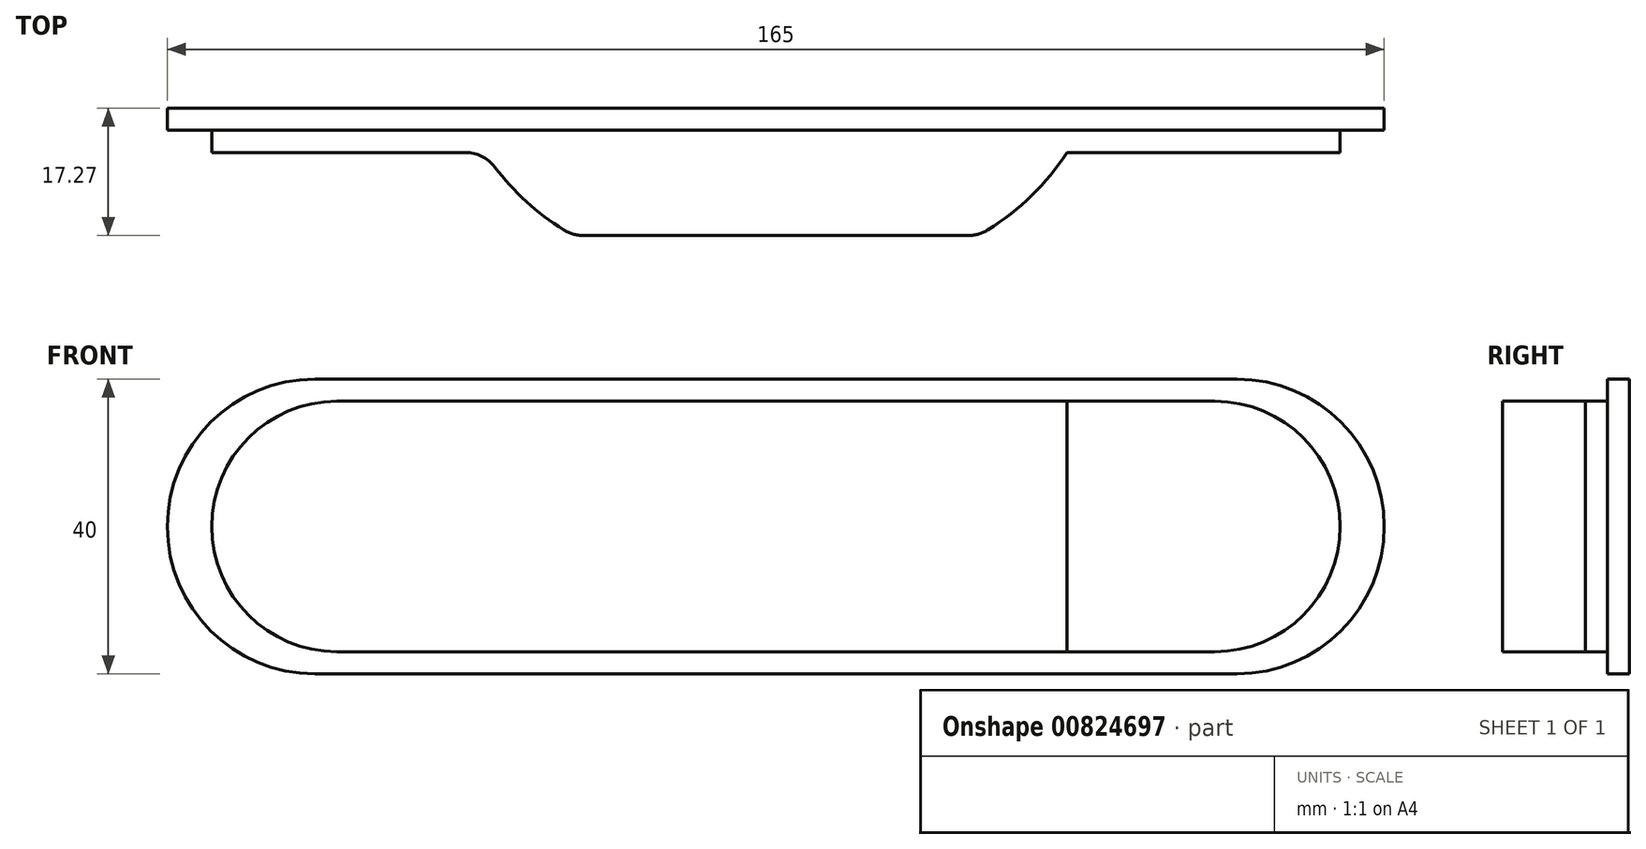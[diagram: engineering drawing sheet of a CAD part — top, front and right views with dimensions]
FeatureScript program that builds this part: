
annotation { "Feature Type Name" : "Feature", "Feature Type Description" : "" }
export const myFeature = defineFeature(function(context is Context, id is Id, definition is map)
    precondition{}
    {
        {
            var Q0;
            Q0=qCreatedBy(makeId("Front.planeOp"),FACE);
            var sketch = newSketch(context, id + "F0", { "sketchPlane" : qUnion([Q0])});
            skLineSegment(sketch, "E0.bottom", {"start": v(62.5, 20) * mm, "end": v(-62.5, 20) * mm});
            skLineSegment(sketch, "E0.top", {"start": v(62.5, -20) * mm, "end": v(-62.5, -20) * mm});
            skLineSegment(sketch, "E0.left", {"start": v(62.5, 20) * mm, "end": v(62.5, -20) * mm});
            skLineSegment(sketch, "E0.right", {"start": v(-62.5, 20) * mm, "end": v(-62.5, -20) * mm});
            skPoint(sketch, "E0.middle", {"position": v(0, 0) * mm});
            skArc(sketch, "E1", {"start": v(-62.5, 20) * mm, "mid": v(-82.5, 0) * mm, "end": v(-62.5, -20) * mm});
            skArc(sketch, "E2", {"start": v(62.5, -20) * mm, "mid": v(82.5, 0) * mm, "end": v(62.5, 20) * mm});
            skSolve(sketch);
        }
        {
            var Q0;
            Q0 = qSketchRegion(id + "F0", true);
            extrude(context, id + "F1", {"entities" : qUnion([Q0]), "depth" : 3 * mm, "offsetDistance" : 25 * mm});
        }
        {
            var Q0;
            Q0=makeQuery(id+"F1.opExtrude","CAP_FACE",FACE,{"disambiguationData":[OSD([sQuery(id+"F0.wireOp",EDGE,"E0.bottom"),sQuery(id+"F0.wireOp",EDGE,"E0.top"),sQuery(id+"F0.wireOp",EDGE,"E1"),sQuery(id+"F0.wireOp",EDGE,"E2")])],"isStart":false});
            var sketch = newSketch(context, id + "F2", { "sketchPlane" : qUnion([Q0])});
            skLineSegment(sketch, "E3.bottom", {"start": v(59.5, 17) * mm, "end": v(-59.5, 17) * mm});
            skLineSegment(sketch, "E3.top", {"start": v(59.5, -17) * mm, "end": v(-59.5, -17) * mm});
            skLineSegment(sketch, "E3.left", {"start": v(59.5, 17) * mm, "end": v(59.5, -17) * mm});
            skLineSegment(sketch, "E3.right", {"start": v(-59.5, 17) * mm, "end": v(-59.5, -17) * mm});
            skPoint(sketch, "E3.middle", {"position": v(0, 0) * mm});
            skArc(sketch, "E4", {"start": v(-59.5, 17) * mm, "mid": v(-76.5, 0) * mm, "end": v(-59.5, -17) * mm});
            skArc(sketch, "E5", {"start": v(59.5, -17) * mm, "mid": v(76.5, 0) * mm, "end": v(59.5, 17) * mm});
            skSolve(sketch);
        }
        {
            var Q0;
            Q0 = qSketchRegion(id + "F2", true);
            extrude(context, id + "F3", {"entities" : qUnion([Q0]), "operationType" : NewBodyOperationType.ADD, "depth" : 3 * mm, "offsetDistance" : 25 * mm});
        }
        {
            var Q0;
            Q0=makeQuery(id+"F3.opExtrude","SWEPT_FACE",FACE,{"disambiguationData":[OSD([sQuery(id+"F2.wireOp",EDGE,"E3.bottom")])]});
            var sketch = newSketch(context, id + "F4", { "sketchPlane" : qUnion([Q0])});
            skLineSegment(sketch, "E6.bottom", {"start": v(-27.5, -17.27) * mm, "end": v(27.5, -17.27) * mm});
            skLineSegment(sketch, "E6.top", {"start": v(-27.5, -2.36) * mm, "end": v(27.5, -2.36) * mm});
            skLineSegment(sketch, "E6.left", {"start": v(-27.5, -17.27) * mm, "end": v(-27.5, -2.36) * mm});
            skLineSegment(sketch, "E6.right", {"start": v(27.5, -17.27) * mm, "end": v(27.5, -2.36) * mm});
            skPoint(sketch, "E6.middle", {"position": v(0, -9.81) * mm});
            skPoint(sketch, "E6.middle.positionSnap0", {"position": v(0, -3) * mm});
            skPoint(sketch, "E6.centerSnap0", {"position": v(0, -3) * mm});
            skArc(sketch, "E7", {"start": v(27.5, -17.27) * mm, "mid": v(34.17, -12.35) * mm, "end": v(39.5, -6) * mm});
            skLineSegment(sketch, "E8", {"start": v(39.5, -6) * mm, "end": v(27.5, -2.36) * mm});
            skArc(sketch, "E9", {"start": v(-39.5, -6) * mm, "mid": v(-34.17, -12.35) * mm, "end": v(-27.5, -17.27) * mm});
            skLineSegment(sketch, "E10", {"start": v(-39.5, -6) * mm, "end": v(-27.5, -2.36) * mm});
            skSolve(sketch);
        }
        {
            var Q0;
            Q0 = qSketchRegion(id + "F4", true);
            extrude(context, id + "F5", {"entities" : qUnion([Q0]), "operationType" : NewBodyOperationType.ADD, "oppositeDirection" : true, "depth" : 34 * mm, "offsetDistance" : 25 * mm});
        }
        {
            var Q0;
            Q0=makeQuery(id+"F5.opExtrude","SWEPT_EDGE",EDGE,{"disambiguationData":[OSD([sQuery(id+"F4.wireOp",EDGE,"E6.bottom"),sQuery(id+"F4.wireOp",EDGE,"E6.left"),sQuery(id+"F4.wireOp",EDGE,"E9")])]});
            var Q1;
            Q1=makeQuery(id+"F5.opExtrude","SWEPT_EDGE",EDGE,{"disambiguationData":[OSD([sQuery(id+"F4.wireOp",EDGE,"E6.bottom"),sQuery(id+"F4.wireOp",EDGE,"E6.right"),sQuery(id+"F4.wireOp",EDGE,"E7")])]});
            var Q2;
            Q2=makeQuery(id+"F5.opExtrude","SWEPT_EDGE",EDGE,{"disambiguationData":[OSD([sQuery(id+"F2.wireOp",EDGE,"E3.bottom"),sQuery(id+"F4.wireOp",EDGE,"E7"),sQuery(id+"F4.wireOp",EDGE,"E8")])]});
            var Q3;
            Q3=makeQuery(id+"F5.opExtrude","SWEPT_EDGE",EDGE,{"disambiguationData":[OSD([sQuery(id+"F2.wireOp",EDGE,"E3.bottom"),sQuery(id+"F4.wireOp",EDGE,"E9"),sQuery(id+"F4.wireOp",EDGE,"E10")])]});
            fillet(context, id + "F6", {"entities" : qUnion([Q0, Q1, Q2, Q3]), "radius" : 5 * mm, "tangentPropagation" : true, "allowEdgeOverflow" : false});
        }
    });
